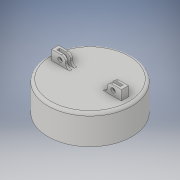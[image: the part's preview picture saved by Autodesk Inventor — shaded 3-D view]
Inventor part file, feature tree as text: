
AUTODESK INVENTOR PART (.ipt)
format: ipt  version: 2018.3 (Build 223284000, 284)  size: 239,104 bytes
history: native  units: in
note: dims shown in document units (in); Inventor stores cm internally (conversion verified against a paired STEP export)
features: extrude x5, sketch x5, plane x2, fillet x2, projected_geometry x1
ambient origin geometry x8: Origin, YZ Plane, XZ Plane, XY Plane, X Axis, Y Axis, Z Axis, Center Point
bodies: Solid1 (feature_tree)
feature tree (15):
  extrude  "Extrusion1"  Depth=1.4961in
  extrude  "Extrusion2"  Depth=1.9685in
  extrude  "Extrusion3"  Depth=1.7913in
  plane  "Work Plane1"
  extrude  "Extrusion4"  Depth=0.0787in TaperAngle=0.0deg
  fillet  "Fillet1"  Radius=2.3622in
  fillet  "Fillet2"  Radius=0.8268in
  plane  "Work Plane2"
  extrude  "Extrusion6"  Depth=1.1024in
  sketch  "Sketch1"  dims[d0=0.126in d1=1.4961in]
  sketch  "Sketch2"  dims[d2=0.2756in d3=1.9685in]
  sketch  "Sketch3"  dims[d4=0.1969in d5=0.0in d6=1.7913in]
  sketch  "Sketch5"  dims[d7=0.0787in d8=0.1969in d9=0.0in d10=2.3622in d11=0.8268in d12=0.0in]
  projected_geometry  "Projected Loop1"
  sketch  "Sketch7"  dims[d13=1.1811in d14=0.1181in d15=0.0787in d16=0.7087in d17=1.1024in d18=1.9685in d19=0.0in d27=0.1969in d28=0.0in]
